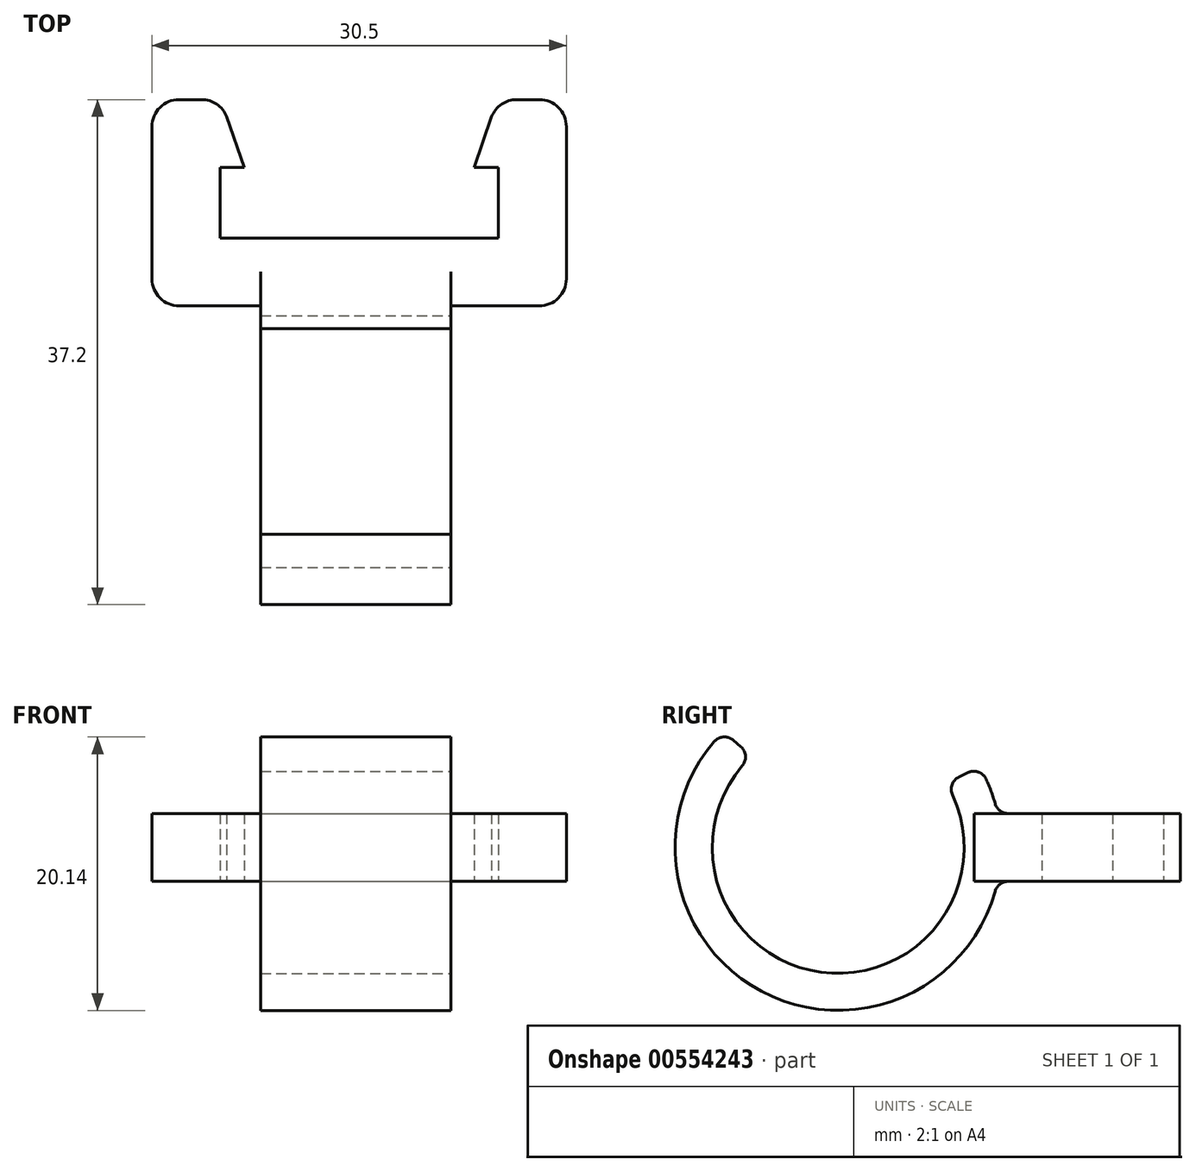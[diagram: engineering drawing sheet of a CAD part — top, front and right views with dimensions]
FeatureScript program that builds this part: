
annotation { "Feature Type Name" : "Feature", "Feature Type Description" : "" }
export const myFeature = defineFeature(function(context is Context, id is Id, definition is map)
    precondition{}
    {
        {
            var Q0;
            Q0=qCreatedBy(makeId("Top.planeOp"),FACE);
            var sketch = newSketch(context, id + "F0", { "sketchPlane" : qUnion([Q0])});
            skLineSegment(sketch, "E0.bottom", {"start": v(0, 0) * mm, "end": v(20.5, 0) * mm});
            skLineSegment(sketch, "E1.left", {"start": v(20.5, 0) * mm, "end": v(20.5, 5.2) * mm});
            skLineSegment(sketch, "E2", {"start": v(25.5, 0) * mm, "end": v(25.5, 8.2) * mm});
            skLineSegment(sketch, "E3", {"start": v(23.5, 10.2) * mm, "end": v(21.85, 10.2) * mm});
            skLineSegment(sketch, "E4", {"start": v(25.5, 0) * mm, "end": v(25.5, -3) * mm});
            skLineSegment(sketch, "E5", {"start": v(23.5, -5) * mm, "end": v(-3, -5) * mm});
            skLineSegment(sketch, "E6", {"start": v(-5, -3) * mm, "end": v(-5, 8.2) * mm});
            skLineSegment(sketch, "E7", {"start": v(-3, 10.2) * mm, "end": v(-1.35, 10.2) * mm});
            skPoint(sketch, "E8.visualSharp", {"position": v(0, 10.2) * mm});
            skArc(sketch, "E8.filletArc", {"start": v(0.5, 8.94) * mm, "mid": v(-0.23, 9.86) * mm, "end": v(-1.35, 10.2) * mm});
            skPoint(sketch, "E9.visualSharp", {"position": v(-5, 10.2) * mm});
            skArc(sketch, "E9.filletArc", {"start": v(-3, 10.2) * mm, "mid": v(-4.41, 9.61) * mm, "end": v(-5, 8.2) * mm});
            skPoint(sketch, "E10.visualSharp", {"position": v(-5, -5) * mm});
            skArc(sketch, "E10.filletArc", {"start": v(-5, -3) * mm, "mid": v(-4.41, -4.41) * mm, "end": v(-3, -5) * mm});
            skPoint(sketch, "E11.visualSharp", {"position": v(25.5, -5) * mm});
            skArc(sketch, "E11.filletArc", {"start": v(23.5, -5) * mm, "mid": v(24.91, -4.41) * mm, "end": v(25.5, -3) * mm});
            skPoint(sketch, "E12.visualSharp", {"position": v(25.5, 10.2) * mm});
            skArc(sketch, "E12.filletArc", {"start": v(25.5, 8.2) * mm, "mid": v(24.91, 9.61) * mm, "end": v(23.5, 10.2) * mm});
            skPoint(sketch, "E13.visualSharp", {"position": v(20.5, 10.2) * mm});
            skArc(sketch, "E13.filletArc", {"start": v(21.85, 10.2) * mm, "mid": v(20.73, 9.86) * mm, "end": v(20, 8.94) * mm});
            skLineSegment(sketch, "E14", {"start": v(0, 0) * mm, "end": v(0, 5.2) * mm});
            skLineSegment(sketch, "E15", {"start": v(0, 5.2) * mm, "end": v(1.8, 5.2) * mm});
            skLineSegment(sketch, "E16", {"start": v(1.8, 5.2) * mm, "end": v(0.5, 8.94) * mm});
            skLineSegment(sketch, "E17", {"start": v(20.5, 5.2) * mm, "end": v(18.7, 5.2) * mm});
            skLineSegment(sketch, "E18", {"start": v(18.7, 5.2) * mm, "end": v(20, 8.94) * mm});
            skSolve(sketch);
        }
        {
            var Q0;
            Q0=makeQuery(id+"F0.imprint","IMPRINT",FACE,{"disambiguationData":[TD([[makeQuery(id+"F0.imprint","IMPRINT",EDGE,{"derivedFrom":sQuery(id+"F0.wireOp",EDGE,"E0.bottom")}),-1.0]])]});
            extrude(context, id + "F1", {"entities" : qUnion([Q0]), "depth" : 5 * mm, "offsetDistance" : 25 * mm});
        }
        {
            var Q0;
            Q0=qCreatedBy(makeId("Front.planeOp"),FACE);
            cPlane(context, id + "F2", {"entities" : qUnion([Q0]), "cplaneType" : CPlaneType.OFFSET, "offset" : 3 * mm, "width" : 150 * mm, "height" : 150 * mm});
        }
        {
            var Q0;
            Q0=qCreatedBy(makeId("Right.planeOp"),FACE);
            cPlane(context, id + "F3", {"entities" : qUnion([Q0]), "cplaneType" : CPlaneType.OFFSET, "offset" : 10 * mm, "width" : 150 * mm, "height" : 150 * mm});
        }
        {
            var Q0;
            Q0=qCreatedBy(id+"F3.planeOp",FACE);
            var sketch = newSketch(context, id + "F4", { "sketchPlane" : qUnion([Q0])});
            skLineSegment(sketch, "E19", {"start": v(0, 0) * mm, "end": v(0, 9.78) * mm, "construction": true});
            skLineSegment(sketch, "E20.0", {"start": v(-5, 0) * mm, "end": v(-5, 9.78) * mm, "construction": true});
            skLineSegment(sketch, "E21", {"start": v(-5, 3.2) * mm, "end": v(-5, 0) * mm});
            skLineSegment(sketch, "E22", {"start": v(-5, 0) * mm, "end": v(-5, 2.5) * mm, "construction": true});
            skLineSegment(sketch, "E23", {"start": v(-3.75, 2.5) * mm, "end": v(-15, 2.5) * mm, "construction": true});
            skLineSegment(sketch, "E24", {"start": v(-6.28, 7.33) * mm, "end": v(-19.74, 9.02) * mm, "construction": true});
            skPoint(sketch, "E25.visualSharp", {"position": v(-3.32, 0) * mm});
            skLineSegment(sketch, "E26", {"start": v(-2.94, 5) * mm, "end": v(-2.94, 5) * mm});
            skPoint(sketch, "E27.visualSharp", {"position": v(-3.32, 5) * mm});
            skArc(sketch, "E28", {"start": v(-24.12, 10.3) * mm, "mid": v(-20.65, -8.09) * mm, "end": v(-3.44, -0.73) * mm});
            skLineSegment(sketch, "E29", {"start": v(-3.26, 5) * mm, "end": v(-3.26, 0) * mm});
            skArc(sketch, "E30.trimOffspring", {"start": v(-3.44, 5.73) * mm, "mid": v(-3.74, 6.65) * mm, "end": v(-4.1, 7.53) * mm});
            skLineSegment(sketch, "E31", {"start": v(-2.48, 5) * mm, "end": v(0, 5) * mm});
            skLineSegment(sketch, "E32", {"start": v(0, 5) * mm, "end": v(0, 0) * mm});
            skPoint(sketch, "E33.visualSharp", {"position": v(-3.26, 5) * mm});
            skArc(sketch, "E33.filletArc", {"start": v(-3.44, 5.73) * mm, "mid": v(-3.08, 5.2) * mm, "end": v(-2.48, 5) * mm});
            skLineSegment(sketch, "E34", {"start": v(0, 0) * mm, "end": v(-2.48, 0) * mm});
            skPoint(sketch, "E35.visualSharp", {"position": v(-3.26, 0) * mm});
            skArc(sketch, "E35.filletArc", {"start": v(-2.48, 0) * mm, "mid": v(-3.08, -0.2) * mm, "end": v(-3.44, -0.73) * mm});
            skPoint(sketch, "E36.visualSharp", {"position": v(-4.8, 8.81) * mm});
            skPoint(sketch, "E37.visualSharp", {"position": v(-23.4, 11.08) * mm});
            skArc(sketch, "E37.filletArc", {"start": v(-22.7, 10.4) * mm, "mid": v(-23.43, 10.64) * mm, "end": v(-24.12, 10.3) * mm});
            skArc(sketch, "E38", {"start": v(-22.06, 8.51) * mm, "mid": v(-16.27, -6.68) * mm, "end": v(-6.58, 6.38) * mm});
            skLineSegment(sketch, "E39", {"start": v(-22.7, 10.4) * mm, "end": v(-22.15, 9.9) * mm});
            skPoint(sketch, "E40.visualSharp", {"position": v(-21.38, 9.22) * mm});
            skArc(sketch, "E40.filletArc", {"start": v(-22.06, 8.51) * mm, "mid": v(-21.82, 9.23) * mm, "end": v(-22.15, 9.9) * mm});
            skPoint(sketch, "E41.visualSharp", {"position": v(-22.86, -2.42) * mm});
            skLineSegment(sketch, "E42", {"start": v(-6.11, 7.7) * mm, "end": v(-5.46, 8.01) * mm});
            skPoint(sketch, "E43.visualSharp", {"position": v(-4.58, 8.44) * mm});
            skArc(sketch, "E43.filletArc", {"start": v(-4.1, 7.53) * mm, "mid": v(-4.68, 8.06) * mm, "end": v(-5.46, 8.01) * mm});
            skPoint(sketch, "E44.visualSharp", {"position": v(-7.03, 7.24) * mm});
            skArc(sketch, "E44.filletArc", {"start": v(-6.11, 7.7) * mm, "mid": v(-6.61, 7.13) * mm, "end": v(-6.58, 6.38) * mm});
            skSolve(sketch);
        }
        {
            var Q0;
            {var subQ1=sQuery(id+"F4.wireOp",EDGE,"E28");Q0=makeQuery(id+"F4.imprint","IMPRINT",FACE,{"disambiguationData":[TD([[makeQuery(id+"F4.imprint","IMPRINT",EDGE,{"derivedFrom":subQ1}),1.0]])]});}
            extrude(context, id + "F5", {"entities" : qUnion([Q0]), "operationType" : NewBodyOperationType.ADD, "oppositeDirection" : true, "depth" : 7 * mm, "offsetDistance" : 25 * mm});
        }
        {
            var Q0;
            {var subQ1=sQuery(id+"F4.wireOp",EDGE,"E28");Q0=makeQuery(id+"F4.imprint","IMPRINT",FACE,{"disambiguationData":[TD([[makeQuery(id+"F4.imprint","IMPRINT",EDGE,{"derivedFrom":subQ1}),1.0]])]});}
            extrude(context, id + "F6", {"entities" : qUnion([Q0]), "operationType" : NewBodyOperationType.ADD, "depth" : 7 * mm, "offsetDistance" : 25 * mm});
        }
    });
